# Revit family: EKF_EE_ГоризонтальныеПланкиПластроновFORT_PROxima
name_source: partatom
category: Электрооборудование
units: mm (PartAtom-declared; Revit-internal decimal feet)

## family parameters
Всегда вертикально = Нет
На основе рабочей плоскости = Да
Общий = Да
При загрузке вырезать с полостями = Нет
Размер круглого соединителя = Использовать диаметр
Тип детали = Силовой щит
Точка расчета площади = Нет

## types (4) — shared parameters
ADSK_Единица измерения = шт.
ADSK_Завод-изготовитель = EKF
ADSK_Количество = 1
ADSK_Марка = Горизонтальные планки для пластронов FORT
ADSK_Материал = Сталь_Оцинкованная
ADSK_Обозначение = Горизонтальные планки для пластронов FORT
ADSK_Размер_Высота = 20 мм
ADSK_Размер_Глубина = 25 мм
Изготовитель = EKF
Серия номенклатуры = PROxima
Степень защиты IP = -
ТВ = EKF_2
Тип установки = -
zero-valued in all types: ADSK_Масса, Отметка по умолчанию

## per-type parameters (varying)
| type | ADSK_Код изделия | ADSK_Размер_Ширина | Тип |
| Горизонтальные планки для пластронов FORT для шкафа шириной 1000мм (2шт.)  EKF PROxima | FKGP10 | 926 мм | 318 мм |
| Горизонтальные планки для пластронов FORT для шкафа шириной 400мм (2шт.)  EKF PROxima | FKGP4 | 326 мм | 319 мм |
| Горизонтальные планки для пластронов FORT для шкафа шириной 600мм (2шт.)  EKF PROxima | FKGP6 | 526 мм | 320 мм |
| Горизонтальные планки для пластронов FORT для шкафа шириной 800мм (2шт.)  EKF PROxima | FKGP8 | 726 мм | 321 мм |

note: column(s) folded — value = type name in every type: ADSK_Наименование
